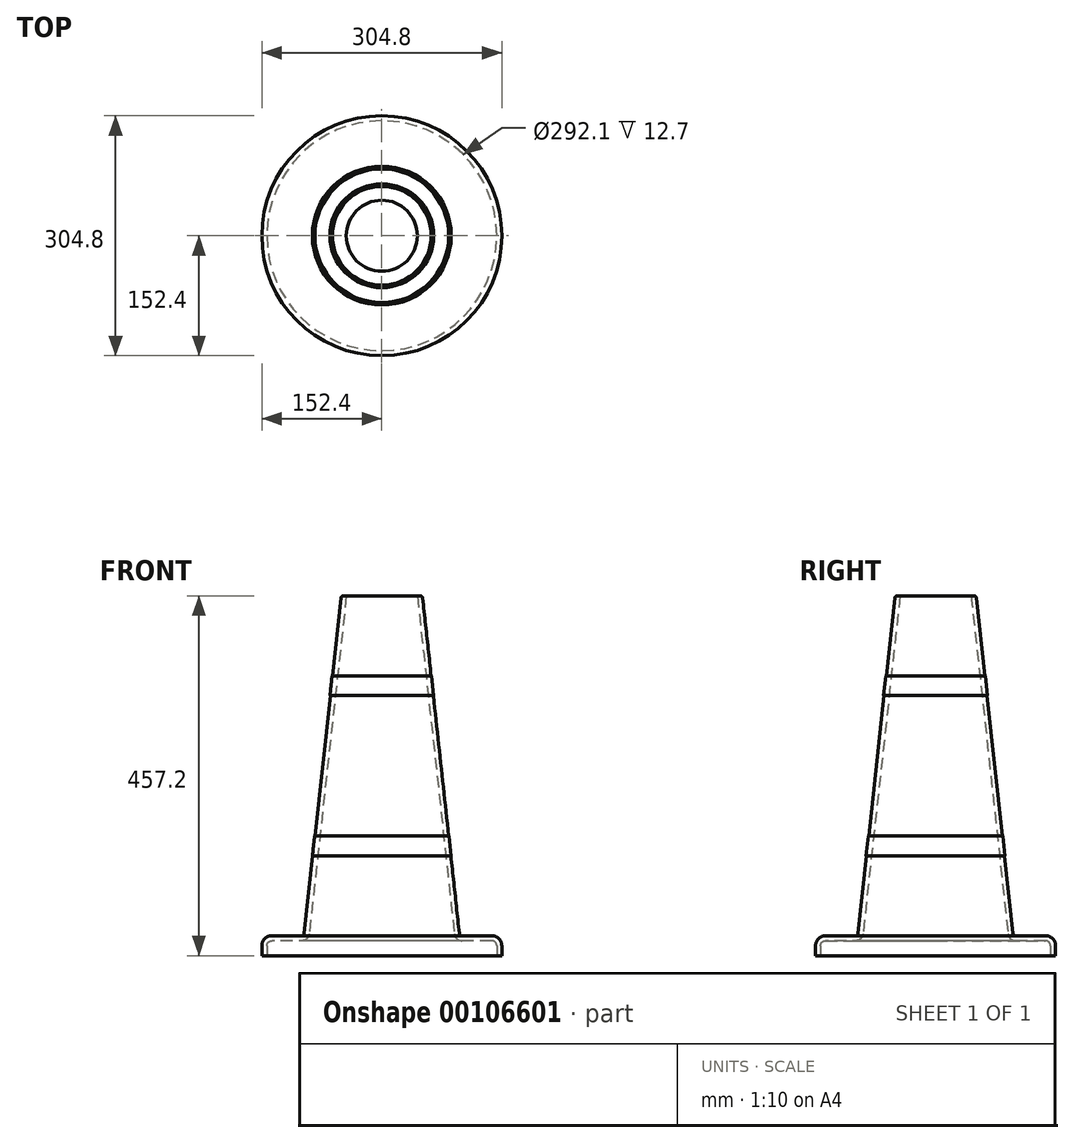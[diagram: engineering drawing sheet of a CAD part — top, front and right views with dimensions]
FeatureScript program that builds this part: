
annotation { "Feature Type Name" : "Feature", "Feature Type Description" : "" }
export const myFeature = defineFeature(function(context is Context, id is Id, definition is map)
    precondition{}
    {
        {
            var Q0;
            Q0=qCreatedBy(makeId("Top.planeOp"),FACE);
            var sketch = newSketch(context, id + "F0", { "sketchPlane" : qUnion([Q0])});
            skCircle(sketch, "E0", {"center": v(0, 0) * mm, "radius": 152.4 * mm});
            skSolve(sketch);
        }
        {
            var Q0;
            Q0 = qSketchRegion(id + "F0", true);
            extrude(context, id + "F1", {"entities" : qUnion([Q0]), "depth" : 25.4 * mm});
        }
        {
            var Q0;
            Q0=qCreatedBy(makeId("Top.planeOp"),FACE);
            var sketch = newSketch(context, id + "F2", { "sketchPlane" : qUnion([Q0])});
            skCircle(sketch, "E1", {"center": v(0, 0) * mm, "radius": 101.6 * mm});
            skSolve(sketch);
        }
        {
            var Q0;
            Q0 = qSketchRegion(id + "F2", true);
            extrude(context, id + "F3", {"entities" : qUnion([Q0]), "operationType" : NewBodyOperationType.ADD, "depth" : 457.2 * mm, "hasDraft" : true, "draftAngle" : 6.25 * degree, "draftPullDirection" : true});
        }
        {
            var Q0;
            Q0=makeQuery(id+"F1.opExtrude","CAP_EDGE",EDGE,{"disambiguationData":[OSD([sQuery(id+"F0.wireOp",EDGE,"E0")])],"isStart":false});
            fillet(context, id + "F4", {"entities" : qUnion([Q0]), "radius" : 12.7 * mm, "tangentPropagation" : true, "allowEdgeOverflow" : false});
        }
        {
            var Q0;
            Q0=makeQuery(id+"F3.opExtrude","CAP_EDGE",EDGE,{"disambiguationData":[OSD([sQuery(id+"F2.wireOp",EDGE,"E1")])],"isStart":false});
            var Q1;
            Q1=makeQuery(id+"F3.boolean.opBoolean","INTERSECT",EDGE,{"derivedFrom":[makeQuery(id+"F1.opExtrude","CAP_FACE",FACE,{"disambiguationData":[OSD([sQuery(id+"F0.wireOp",EDGE,"E0")])],"isStart":false}),makeQuery(id+"F3.opExtrude","SWEPT_FACE",FACE,{"disambiguationData":[OSD([sQuery(id+"F2.wireOp",EDGE,"E1")])]})]});
            fillet(context, id + "F5", {"entities" : qUnion([Q0, Q1]), "radius" : 3.17 * mm, "tangentPropagation" : true, "allowEdgeOverflow" : false});
        }
        {
            var Q0;
            Q0=makeQuery(id+"F1.opExtrude","CAP_FACE",FACE,{"disambiguationData":[OSD([sQuery(id+"F0.wireOp",EDGE,"E0")])],"isStart":true});
            var Q1;
            Q1=makeQuery(id+"F3.opExtrude","CAP_FACE",FACE,{"disambiguationData":[OSD([sQuery(id+"F2.wireOp",EDGE,"E1")])],"isStart":false});
            shell(context, id + "F6", {"entities" : qUnion([Q0, Q1]), "thickness" : 6.35 * mm});
        }
        {
            var Q0;
            Q0=qCreatedBy(makeId("Front.planeOp"),FACE);
            var sketch = newSketch(context, id + "F7", { "sketchPlane" : qUnion([Q0])});
            skLineSegment(sketch, "E2", {"start": v(0, 0) * mm, "end": v(0, 488.88) * mm, "construction": true});
            skSolve(sketch);
        }
        {
            var Q0;
            Q0=qCreatedBy(makeId("Front.planeOp"),FACE);
            var sketch = newSketch(context, id + "F8", { "sketchPlane" : qUnion([Q0])});
            skLineSegment(sketch, "E3", {"start": v(-116.02, 127) * mm, "end": v(128.18, 127) * mm, "construction": true});
            skLineSegment(sketch, "E4", {"start": v(62.78, 355.56) * mm, "end": v(65.52, 330.35) * mm});
            skLineSegment(sketch, "E5", {"start": v(87.74, 127) * mm, "end": v(84.94, 152.2) * mm});
            skLineSegment(sketch, "E6", {"start": v(84.94, 152.2) * mm, "end": v(85.32, 152.24) * mm});
            skLineSegment(sketch, "E7", {"start": v(85.32, 152.24) * mm, "end": v(88.12, 127) * mm});
            skLineSegment(sketch, "E8", {"start": v(88.12, 127) * mm, "end": v(87.74, 127) * mm});
            skLineSegment(sketch, "E9", {"start": v(62.78, 355.56) * mm, "end": v(63.15, 355.6) * mm});
            skLineSegment(sketch, "E10", {"start": v(63.15, 355.6) * mm, "end": v(65.9, 330.35) * mm});
            skLineSegment(sketch, "E11", {"start": v(65.9, 330.35) * mm, "end": v(65.52, 330.35) * mm});
            skLineSegment(sketch, "E12", {"start": v(-73.98, 355.6) * mm, "end": v(96.17, 355.6) * mm, "construction": true});
            skSolve(sketch);
        }
        {
            var Q0;
            Q0 = qSketchRegion(id + "F8", true);
            var Q1;
            Q1=sQuery(id+"F7.wireOp",EDGE,"E2");
            revolve(context, id + "F9", {"operationType" : NewBodyOperationType.ADD, "entities" : qUnion([Q0]), "axis" : qUnion([Q1]), "revolveType" : RevolveType.FULL});
        }
    });
